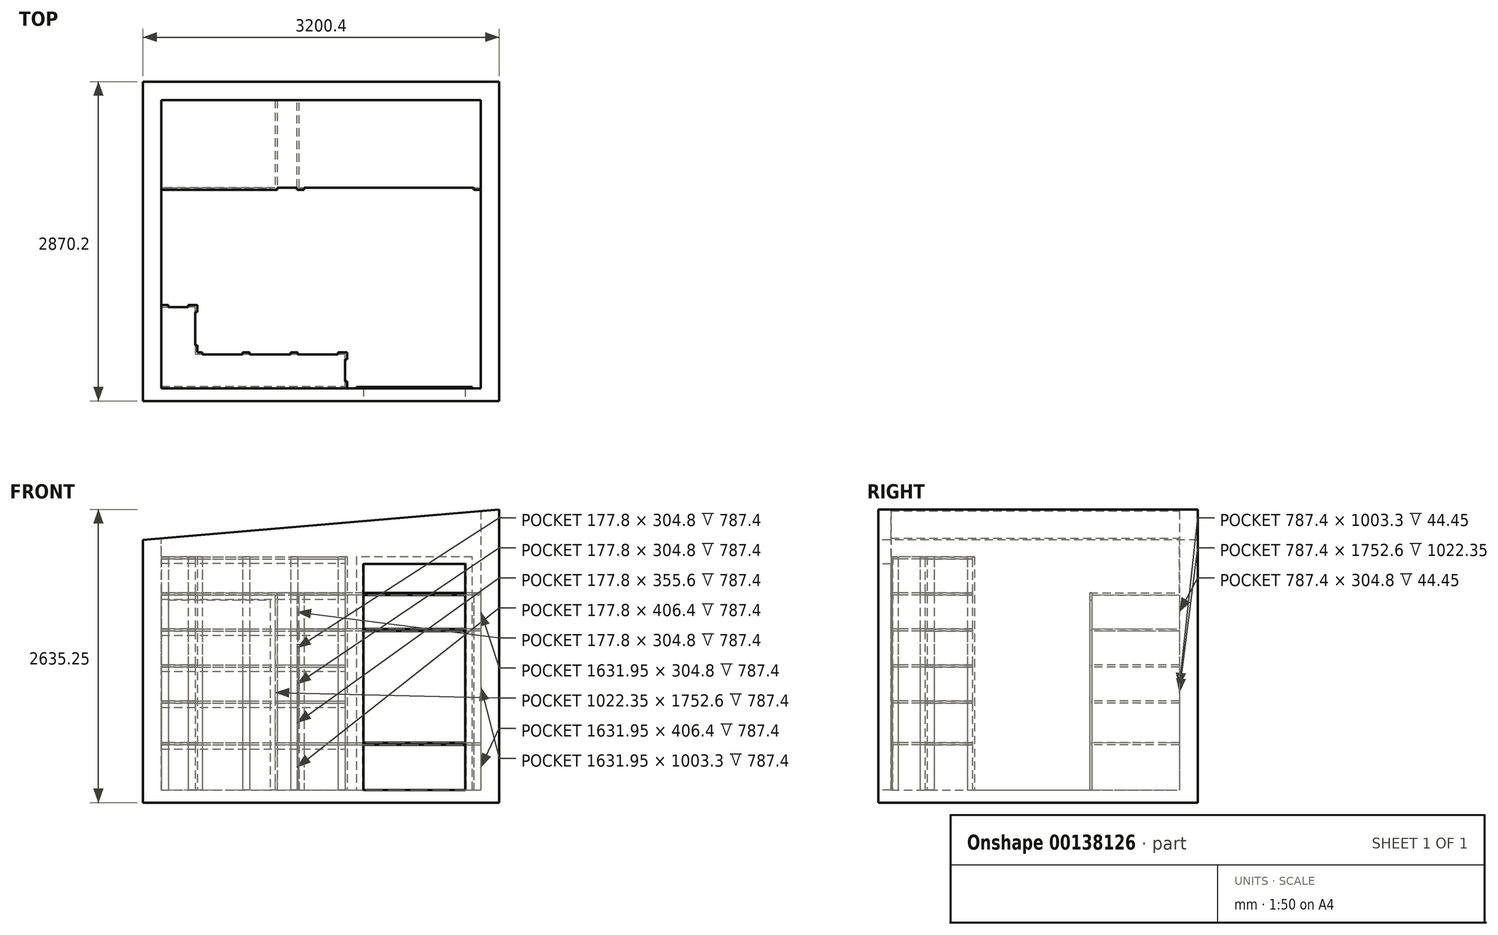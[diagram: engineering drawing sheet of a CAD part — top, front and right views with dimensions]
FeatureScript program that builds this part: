
annotation { "Feature Type Name" : "Feature", "Feature Type Description" : "" }
export const myFeature = defineFeature(function(context is Context, id is Id, definition is map)
    precondition{}
    {
        {
            var Q0;
            Q0=qCreatedBy(makeId("Right.planeOp"),FACE);
            var sketch = newSketch(context, id + "F0", { "sketchPlane" : qUnion([Q0])});
            skLineSegment(sketch, "E0.bottom", {"start": v(0, 0) * mm, "end": v(2590.8, 0) * mm});
            skLineSegment(sketch, "E0.top", {"start": v(0, 2520.95) * mm, "end": v(2590.8, 2520.95) * mm});
            skLineSegment(sketch, "E0.left", {"start": v(0, 0) * mm, "end": v(0, 2520.95) * mm});
            skLineSegment(sketch, "E0.right", {"start": v(2590.8, 0) * mm, "end": v(2590.8, 2520.95) * mm});
            skSolve(sketch);
        }
        {
            var Q0;
            Q0=qSketchRegion(id+"F0",true);
            extrude(context, id + "F1", {"entities" : qUnion([Q0]), "depth" : 165.1 * mm});
        }
        {
            var Q0;
            Q0=makeQuery(id+"F1.opExtrude","SWEPT_FACE",FACE,{"disambiguationData":[OSD([sQuery(id+"F0.wireOp",EDGE,"E0.left")])]});
            var sketch = newSketch(context, id + "F2", { "sketchPlane" : qUnion([Q0])});
            skLineSegment(sketch, "E1.bottom", {"start": v(0, 2520.95) * mm, "end": v(3035.3, 2520.95) * mm});
            skLineSegment(sketch, "E1.top", {"start": v(0, 0) * mm, "end": v(3035.3, 0) * mm});
            skLineSegment(sketch, "E1.left", {"start": v(0, 2520.95) * mm, "end": v(0, 0) * mm});
            skLineSegment(sketch, "E1.right", {"start": v(3035.3, 2520.95) * mm, "end": v(3035.3, 0) * mm});
            skSolve(sketch);
        }
        {
            var Q0;
            Q0=qSketchRegion(id+"F2",true);
            extrude(context, id + "F3", {"entities" : qUnion([Q0]), "operationType" : NewBodyOperationType.ADD, "depth" : 114.3 * mm});
        }
        {
            var Q0;
            Q0=makeQuery(id+"F1.opExtrude","SWEPT_FACE",FACE,{"disambiguationData":[OSD([sQuery(id+"F0.wireOp",EDGE,"E0.right")])]});
            var sketch = newSketch(context, id + "F4", { "sketchPlane" : qUnion([Q0])});
            skLineSegment(sketch, "E2.bottom", {"start": v(0, 2520.95) * mm, "end": v(-3035.3, 2520.95) * mm});
            skLineSegment(sketch, "E2.top", {"start": v(0, 0) * mm, "end": v(-3035.3, 0) * mm});
            skLineSegment(sketch, "E2.left", {"start": v(0, 2520.95) * mm, "end": v(0, 0) * mm});
            skLineSegment(sketch, "E2.right", {"start": v(-3035.3, 2520.95) * mm, "end": v(-3035.3, 0) * mm});
            skSolve(sketch);
        }
        {
            var Q0;
            Q0=qSketchRegion(id+"F4",true);
            extrude(context, id + "F5", {"entities" : qUnion([Q0]), "operationType" : NewBodyOperationType.ADD, "depth" : 165.1 * mm});
        }
        {
            var Q0;
            Q0=makeQuery(id+"F3.opExtrude","SWEPT_FACE",FACE,{"disambiguationData":[OSD([sQuery(id+"F2.wireOp",EDGE,"E1.right")])]});
            var sketch = newSketch(context, id + "F6", { "sketchPlane" : qUnion([Q0])});
            skLineSegment(sketch, "E3.bottom", {"start": v(-114.3, 2520.95) * mm, "end": v(2755.9, 2520.95) * mm});
            skLineSegment(sketch, "E3.top", {"start": v(-114.3, 0) * mm, "end": v(2755.9, 0) * mm});
            skLineSegment(sketch, "E3.left", {"start": v(-114.3, 2520.95) * mm, "end": v(-114.3, 0) * mm});
            skLineSegment(sketch, "E3.right", {"start": v(2755.9, 2520.95) * mm, "end": v(2755.9, 0) * mm});
            skSolve(sketch);
        }
        {
            var Q0;
            Q0=qSketchRegion(id+"F6",true);
            extrude(context, id + "F7", {"entities" : qUnion([Q0]), "operationType" : NewBodyOperationType.ADD, "depth" : 165.1 * mm});
        }
        {
            var Q0;
            Q0=makeQuery(id+"F7.boolean.opBoolean","MERGE",FACE,{"derivedFrom":[makeQuery(id+"F3.opExtrude","CAP_FACE",FACE,{"disambiguationData":[OSD([sQuery(id+"F2.wireOp",EDGE,"E1.bottom"),sQuery(id+"F2.wireOp",EDGE,"E1.top"),sQuery(id+"F2.wireOp",EDGE,"E1.left"),sQuery(id+"F2.wireOp",EDGE,"E1.right")])],"isStart":false}),makeQuery(id+"F7.opExtrude","SWEPT_FACE",FACE,{"disambiguationData":[OSD([sQuery(id+"F6.wireOp",EDGE,"E3.left")])]})]});
            var sketch = newSketch(context, id + "F8", { "sketchPlane" : qUnion([Q0])});
            skLineSegment(sketch, "E4.bottom", {"start": v(2895.6, 0) * mm, "end": v(1981.2, 0) * mm});
            skLineSegment(sketch, "E4.top", {"start": v(2895.6, 2032) * mm, "end": v(1981.2, 2032) * mm});
            skLineSegment(sketch, "E4.left", {"start": v(2895.6, 0) * mm, "end": v(2895.6, 2032) * mm});
            skLineSegment(sketch, "E4.right", {"start": v(1981.2, 0) * mm, "end": v(1981.2, 2032) * mm});
            skSolve(sketch);
        }
        {
            var Q0;
            Q0=makeQuery(id+"F8.imprint","IMPRINT",FACE,{"disambiguationData":[TD([[makeQuery(id+"F8.imprint","IMPRINT",EDGE,{"derivedFrom":sQuery(id+"F8.wireOp",EDGE,"E4.top")}),-1.0]])]});
            var sketch = newSketch(context, id + "F9", { "sketchPlane" : qUnion([Q0])});
            skLineSegment(sketch, "E5", {"start": v(0, 2247.9) * mm, "end": v(3200.4, 2520.95) * mm});
            skLineSegment(sketch, "E6", {"start": v(3200.4, 2520.95) * mm, "end": v(0, 2520.95) * mm});
            skLineSegment(sketch, "E7", {"start": v(0, 2520.95) * mm, "end": v(0, 2247.9) * mm});
            skSolve(sketch);
        }
        {
            var Q0;
            Q0=qSketchRegion(id+"F9",true);
            extrude(context, id + "F10", {"entities" : qUnion([Q0]), "operationType" : NewBodyOperationType.REMOVE, "endBound" : BoundingType.THROUGH_ALL, "oppositeDirection" : true, "depth" : 25.4 * mm});
        }
        {
            var Q0;
            Q0=qSketchRegion(id+"F8",true);
            extrude(context, id + "F11", {"entities" : qUnion([Q0]), "operationType" : NewBodyOperationType.REMOVE, "oppositeDirection" : true, "depth" : 114.3 * mm});
        }
        {
            var Q0;
            Q0=makeQuery(id+"F7.boolean.opBoolean","MERGE",FACE,{"derivedFrom":[makeQuery(id+"F5.boolean.opBoolean","MERGE",FACE,{"derivedFrom":[makeQuery(id+"F3.boolean.opBoolean","MERGE",FACE,{"derivedFrom":[makeQuery(id+"F1.opExtrude","SWEPT_FACE",FACE,{"disambiguationData":[OSD([sQuery(id+"F0.wireOp",EDGE,"E0.bottom")])]}),makeQuery(id+"F3.opExtrude","SWEPT_FACE",FACE,{"disambiguationData":[OSD([sQuery(id+"F2.wireOp",EDGE,"E1.top")])]})]}),makeQuery(id+"F5.opExtrude","SWEPT_FACE",FACE,{"disambiguationData":[OSD([sQuery(id+"F4.wireOp",EDGE,"E2.top")])]})]}),makeQuery(id+"F7.opExtrude","SWEPT_FACE",FACE,{"disambiguationData":[OSD([sQuery(id+"F6.wireOp",EDGE,"E3.top")])]})]});
            var sketch = newSketch(context, id + "F12", { "sketchPlane" : qUnion([Q0])});
            skLineSegment(sketch, "E8.bottom", {"start": v(0, 114.3) * mm, "end": v(3200.4, 114.3) * mm});
            skLineSegment(sketch, "E8.top", {"start": v(0, -2755.9) * mm, "end": v(3200.4, -2755.9) * mm});
            skLineSegment(sketch, "E8.left", {"start": v(0, 114.3) * mm, "end": v(0, -2755.9) * mm});
            skLineSegment(sketch, "E8.right", {"start": v(3200.4, 114.3) * mm, "end": v(3200.4, -2755.9) * mm});
            skSolve(sketch);
        }
        {
            var Q0;
            Q0=qSketchRegion(id+"F12",true);
            extrude(context, id + "F13", {"entities" : qUnion([Q0]), "operationType" : NewBodyOperationType.ADD, "depth" : 114.3 * mm});
        }
        {
            var Q0;
            Q0=makeQuery(id+"F3.opExtrude","CAP_FACE",FACE,{"disambiguationData":[OSD([sQuery(id+"F2.wireOp",EDGE,"E1.bottom"),sQuery(id+"F2.wireOp",EDGE,"E1.top"),sQuery(id+"F2.wireOp",EDGE,"E1.left"),sQuery(id+"F2.wireOp",EDGE,"E1.right")])],"isStart":true});
            var sketch = newSketch(context, id + "F14", { "sketchPlane" : qUnion([Q0])});
            skLineSegment(sketch, "E9", {"start": v(-1974.85, 0) * mm, "end": v(-1974.85, 2038.35) * mm});
            skLineSegment(sketch, "E10", {"start": v(-1974.85, 2038.35) * mm, "end": v(-2901.95, 2038.35) * mm});
            skLineSegment(sketch, "E11", {"start": v(-2901.95, 2038.35) * mm, "end": v(-2901.95, 0) * mm});
            skPoint(sketch, "E11.endSnap0", {"position": v(-2965.45, 0) * mm});
            skLineSegment(sketch, "E12", {"start": v(-2901.95, 0) * mm, "end": v(-2959.1, 0) * mm});
            skLineSegment(sketch, "E13", {"start": v(-2959.1, 0) * mm, "end": v(-2959.1, 2095.5) * mm});
            skLineSegment(sketch, "E14", {"start": v(-2959.1, 2095.5) * mm, "end": v(-1917.7, 2095.5) * mm});
            skLineSegment(sketch, "E15", {"start": v(-1917.7, 2095.5) * mm, "end": v(-1917.7, 0) * mm});
            skLineSegment(sketch, "E16", {"start": v(-1917.7, 0) * mm, "end": v(-1974.85, 0) * mm});
            skSolve(sketch);
        }
        {
            var Q0;
            Q0=qSketchRegion(id+"F14",true);
            extrude(context, id + "F15", {"entities" : qUnion([Q0]), "operationType" : NewBodyOperationType.ADD, "depth" : 12.7 * mm});
        }
        {
            var Q0;
            Q0=makeQuery(id+"F15.boolean.opBoolean","SPLIT",FACE,{"disambiguationData":[TD([makeQuery(id+"F10.boolean.opBoolean","COPY",FACE,{"derivedFrom":makeQuery(id+"F10.opExtrude","SWEPT_FACE",FACE,{"disambiguationData":[OSD([sQuery(id+"F9.wireOp",EDGE,"E5")])]})})])],"derivedFrom":makeQuery(id+"F3.opExtrude","CAP_FACE",FACE,{"disambiguationData":[OSD([sQuery(id+"F2.wireOp",EDGE,"E1.bottom"),sQuery(id+"F2.wireOp",EDGE,"E1.top"),sQuery(id+"F2.wireOp",EDGE,"E1.left"),sQuery(id+"F2.wireOp",EDGE,"E1.right")])],"isStart":true})});
            var Q1;
            Q1=makeQuery(id+"F13.boolean.opBoolean","MERGE",FACE,{"derivedFrom":[makeQuery(id+"F7.boolean.opBoolean","MERGE",FACE,{"derivedFrom":[makeQuery(id+"F3.opExtrude","CAP_FACE",FACE,{"disambiguationData":[OSD([sQuery(id+"F2.wireOp",EDGE,"E1.bottom"),sQuery(id+"F2.wireOp",EDGE,"E1.top"),sQuery(id+"F2.wireOp",EDGE,"E1.left"),sQuery(id+"F2.wireOp",EDGE,"E1.right")])],"isStart":false}),makeQuery(id+"F7.opExtrude","SWEPT_FACE",FACE,{"disambiguationData":[OSD([sQuery(id+"F6.wireOp",EDGE,"E3.left")])]})]}),makeQuery(id+"F13.opExtrude","SWEPT_FACE",FACE,{"disambiguationData":[OSD([sQuery(id+"F12.wireOp",EDGE,"E8.bottom")])]})]});
            cPlane(context, id + "F16", {"entities" : qUnion([Q0, Q1]), "cplaneType" : CPlaneType.MID_PLANE, "offset" : 25.4 * mm, "width" : 152.4 * mm, "height" : 152.4 * mm});
        }
        {
            var Q0;
            Q0=makeQuery(id+"F13.opExtrude","CAP_FACE",FACE,{"disambiguationData":[OSD([sQuery(id+"F12.wireOp",EDGE,"E8.bottom"),sQuery(id+"F12.wireOp",EDGE,"E8.top"),sQuery(id+"F12.wireOp",EDGE,"E8.left"),sQuery(id+"F12.wireOp",EDGE,"E8.right")])],"isStart":true});
            var sketch = newSketch(context, id + "F17", { "sketchPlane" : qUnion([Q0])});
            skLineSegment(sketch, "E17.bottom", {"start": v(3200.4, 304.8) * mm, "end": v(469.9, 304.8) * mm});
            skLineSegment(sketch, "E17.top", {"start": v(3200.4, 2755.9) * mm, "end": v(469.9, 2755.9) * mm});
            skLineSegment(sketch, "E17.left", {"start": v(3200.4, 304.8) * mm, "end": v(3200.4, 2755.9) * mm});
            skLineSegment(sketch, "E17.right", {"start": v(469.9, 304.8) * mm, "end": v(469.9, 2755.9) * mm});
            skSolve(sketch);
        }
        {
            var Q0;
            Q0=makeQuery(id+"F15.boolean.opBoolean","SPLIT",FACE,{"disambiguationData":[TD([makeQuery(id+"F10.boolean.opBoolean","COPY",FACE,{"derivedFrom":makeQuery(id+"F10.opExtrude","SWEPT_FACE",FACE,{"disambiguationData":[OSD([sQuery(id+"F9.wireOp",EDGE,"E5")])]})})])],"derivedFrom":makeQuery(id+"F3.opExtrude","CAP_FACE",FACE,{"disambiguationData":[OSD([sQuery(id+"F2.wireOp",EDGE,"E1.bottom"),sQuery(id+"F2.wireOp",EDGE,"E1.top"),sQuery(id+"F2.wireOp",EDGE,"E1.left"),sQuery(id+"F2.wireOp",EDGE,"E1.right")])],"isStart":true})});
            var sketch = newSketch(context, id + "F18", { "sketchPlane" : qUnion([Q0])});
            skLineSegment(sketch, "E18.bottom", {"start": v(-165.1, 406.4) * mm, "end": v(-1816.1, 406.4) * mm});
            skLineSegment(sketch, "E18.top", {"start": v(-165.1, 425.45) * mm, "end": v(-1816.1, 425.45) * mm});
            skLineSegment(sketch, "E18.left", {"start": v(-165.1, 406.4) * mm, "end": v(-165.1, 425.45) * mm});
            skLineSegment(sketch, "E18.right", {"start": v(-1816.1, 406.4) * mm, "end": v(-1816.1, 425.45) * mm});
            skLineSegment(sketch, "E19.bottom", {"start": v(-165.1, 781.05) * mm, "end": v(-1816.1, 781.05) * mm});
            skLineSegment(sketch, "E19.top", {"start": v(-165.1, 800.1) * mm, "end": v(-1816.1, 800.1) * mm});
            skLineSegment(sketch, "E19.left", {"start": v(-165.1, 781.05) * mm, "end": v(-165.1, 800.1) * mm});
            skLineSegment(sketch, "E19.right", {"start": v(-1816.1, 781.05) * mm, "end": v(-1816.1, 800.1) * mm});
            skLineSegment(sketch, "E20.bottom", {"start": v(-165.1, 1104.9) * mm, "end": v(-1816.1, 1104.9) * mm});
            skLineSegment(sketch, "E20.top", {"start": v(-165.1, 1123.95) * mm, "end": v(-1816.1, 1123.95) * mm});
            skLineSegment(sketch, "E20.left", {"start": v(-165.1, 1104.9) * mm, "end": v(-165.1, 1123.95) * mm});
            skLineSegment(sketch, "E20.right", {"start": v(-1816.1, 1104.9) * mm, "end": v(-1816.1, 1123.95) * mm});
            skLineSegment(sketch, "E21.bottom", {"start": v(-165.1, 1428.75) * mm, "end": v(-1816.1, 1428.75) * mm});
            skLineSegment(sketch, "E21.top", {"start": v(-165.1, 1447.8) * mm, "end": v(-1816.1, 1447.8) * mm});
            skLineSegment(sketch, "E21.left", {"start": v(-165.1, 1428.75) * mm, "end": v(-165.1, 1447.8) * mm});
            skLineSegment(sketch, "E21.right", {"start": v(-1816.1, 1428.75) * mm, "end": v(-1816.1, 1447.8) * mm});
            skLineSegment(sketch, "E22.bottom", {"start": v(-165.1, 1752.6) * mm, "end": v(-1816.1, 1752.6) * mm});
            skLineSegment(sketch, "E22.top", {"start": v(-165.1, 1771.65) * mm, "end": v(-1816.1, 1771.65) * mm});
            skLineSegment(sketch, "E22.left", {"start": v(-165.1, 1752.6) * mm, "end": v(-165.1, 1771.65) * mm});
            skLineSegment(sketch, "E22.right", {"start": v(-1816.1, 1752.6) * mm, "end": v(-1816.1, 1771.65) * mm});
            skLineSegment(sketch, "E23.bottom", {"start": v(-165.1, 2076.45) * mm, "end": v(-1816.1, 2076.45) * mm});
            skLineSegment(sketch, "E23.top", {"start": v(-165.1, 2095.5) * mm, "end": v(-1816.1, 2095.5) * mm});
            skLineSegment(sketch, "E23.left", {"start": v(-165.1, 2076.45) * mm, "end": v(-165.1, 2095.5) * mm});
            skLineSegment(sketch, "E23.right", {"start": v(-1816.1, 2076.45) * mm, "end": v(-1816.1, 2095.5) * mm});
            skSolve(sketch);
        }
        {
            var Q0;
            Q0=qSketchRegion(id+"F18",true);
            extrude(context, id + "F19", {"entities" : qUnion([Q0]), "operationType" : NewBodyOperationType.ADD, "depth" : 304.8 * mm});
        }
        {
            var Q0;
            Q0=makeQuery(id+"F15.boolean.opBoolean","SPLIT",FACE,{"disambiguationData":[TD([makeQuery(id+"F10.boolean.opBoolean","COPY",FACE,{"derivedFrom":makeQuery(id+"F10.opExtrude","SWEPT_FACE",FACE,{"disambiguationData":[OSD([sQuery(id+"F9.wireOp",EDGE,"E5")])]})})])],"derivedFrom":makeQuery(id+"F3.opExtrude","CAP_FACE",FACE,{"disambiguationData":[OSD([sQuery(id+"F2.wireOp",EDGE,"E1.bottom"),sQuery(id+"F2.wireOp",EDGE,"E1.top"),sQuery(id+"F2.wireOp",EDGE,"E1.left"),sQuery(id+"F2.wireOp",EDGE,"E1.right")])],"isStart":true})});
            var sketch = newSketch(context, id + "F20", { "sketchPlane" : qUnion([Q0])});
            skLineSegment(sketch, "E24.bottom", {"start": v(-165.1, 2076.45) * mm, "end": v(-1816.1, 2076.45) * mm});
            skLineSegment(sketch, "E24.top", {"start": v(-165.1, 2038.35) * mm, "end": v(-1816.1, 2038.35) * mm});
            skLineSegment(sketch, "E24.left", {"start": v(-165.1, 2076.45) * mm, "end": v(-165.1, 2038.35) * mm});
            skLineSegment(sketch, "E24.right", {"start": v(-1816.1, 2076.45) * mm, "end": v(-1816.1, 2038.35) * mm});
            skLineSegment(sketch, "E25.bottom", {"start": v(-165.1, 1752.6) * mm, "end": v(-1816.1, 1752.6) * mm});
            skLineSegment(sketch, "E25.top", {"start": v(-165.1, 1714.5) * mm, "end": v(-1816.1, 1714.5) * mm});
            skLineSegment(sketch, "E25.left", {"start": v(-165.1, 1752.6) * mm, "end": v(-165.1, 1714.5) * mm});
            skLineSegment(sketch, "E25.right", {"start": v(-1816.1, 1752.6) * mm, "end": v(-1816.1, 1714.5) * mm});
            skLineSegment(sketch, "E26.bottom", {"start": v(-165.1, 1428.75) * mm, "end": v(-1816.1, 1428.75) * mm});
            skLineSegment(sketch, "E26.top", {"start": v(-165.1, 1390.65) * mm, "end": v(-1816.1, 1390.65) * mm});
            skLineSegment(sketch, "E26.left", {"start": v(-165.1, 1428.75) * mm, "end": v(-165.1, 1390.65) * mm});
            skLineSegment(sketch, "E26.right", {"start": v(-1816.1, 1428.75) * mm, "end": v(-1816.1, 1390.65) * mm});
            skLineSegment(sketch, "E27.bottom", {"start": v(-165.1, 1104.9) * mm, "end": v(-1816.1, 1104.9) * mm});
            skLineSegment(sketch, "E27.top", {"start": v(-165.1, 1066.8) * mm, "end": v(-1816.1, 1066.8) * mm});
            skLineSegment(sketch, "E27.left", {"start": v(-165.1, 1104.9) * mm, "end": v(-165.1, 1066.8) * mm});
            skLineSegment(sketch, "E27.right", {"start": v(-1816.1, 1104.9) * mm, "end": v(-1816.1, 1066.8) * mm});
            skLineSegment(sketch, "E28.bottom", {"start": v(-165.1, 406.4) * mm, "end": v(-1816.1, 406.4) * mm});
            skLineSegment(sketch, "E28.top", {"start": v(-165.1, 368.3) * mm, "end": v(-1816.1, 368.3) * mm});
            skLineSegment(sketch, "E28.left", {"start": v(-165.1, 406.4) * mm, "end": v(-165.1, 368.3) * mm});
            skLineSegment(sketch, "E28.right", {"start": v(-1816.1, 406.4) * mm, "end": v(-1816.1, 368.3) * mm});
            skLineSegment(sketch, "E29.bottom", {"start": v(-165.1, 781.05) * mm, "end": v(-1816.1, 781.05) * mm});
            skLineSegment(sketch, "E29.top", {"start": v(-165.1, 742.95) * mm, "end": v(-1816.1, 742.95) * mm});
            skLineSegment(sketch, "E29.left", {"start": v(-165.1, 781.05) * mm, "end": v(-165.1, 742.95) * mm});
            skLineSegment(sketch, "E29.right", {"start": v(-1816.1, 781.05) * mm, "end": v(-1816.1, 742.95) * mm});
            skSolve(sketch);
        }
        {
            var Q0;
            Q0=qSketchRegion(id+"F20",true);
            extrude(context, id + "F21", {"entities" : qUnion([Q0]), "operationType" : NewBodyOperationType.ADD, "depth" : 19.05 * mm});
        }
        {
            var Q0;
            Q0=makeQuery(id+"Fllte4z2JdaSj08_1.boolean.opBoolean","MERGE",FACE,{"derivedFrom":[makeQuery(id+"F13.opExtrude","CAP_FACE",FACE,{"disambiguationData":[OSD([sQuery(id+"F12.wireOp",EDGE,"E8.bottom"),sQuery(id+"F12.wireOp",EDGE,"E8.top"),sQuery(id+"F12.wireOp",EDGE,"E8.left"),sQuery(id+"F12.wireOp",EDGE,"E8.right")])],"isStart":true}),makeQuery(id+"Fllte4z2JdaSj08_1.opExtrude","CAP_FACE",FACE,{"disambiguationData":[OSD([sQuery(id+"F17.wireOp",EDGE,"E17.bottom"),sQuery(id+"F17.wireOp",EDGE,"E17.top"),sQuery(id+"F17.wireOp",EDGE,"E17.left"),sQuery(id+"F17.wireOp",EDGE,"E17.right")])],"isStart":true})]});
            var sketch = newSketch(context, id + "F22", { "sketchPlane" : qUnion([Q0])});
            skLineSegment(sketch, "E30.bottom", {"start": v(1835.15, 0) * mm, "end": v(1816.1, 0) * mm});
            skLineSegment(sketch, "E30.top", {"start": v(1835.15, 63.5) * mm, "end": v(1816.1, 63.5) * mm});
            skLineSegment(sketch, "E30.left", {"start": v(1835.15, 0) * mm, "end": v(1835.15, 63.5) * mm});
            skLineSegment(sketch, "E30.right", {"start": v(1816.1, 0) * mm, "end": v(1816.1, 63.5) * mm});
            skLineSegment(sketch, "E31.bottom", {"start": v(1835.15, 260.35) * mm, "end": v(1816.1, 260.35) * mm});
            skLineSegment(sketch, "E31.top", {"start": v(1835.15, 323.85) * mm, "end": v(1816.1, 323.85) * mm});
            skLineSegment(sketch, "E31.left", {"start": v(1835.15, 260.35) * mm, "end": v(1835.15, 323.85) * mm});
            skLineSegment(sketch, "E31.right", {"start": v(1816.1, 260.35) * mm, "end": v(1816.1, 323.85) * mm});
            skLineSegment(sketch, "E32.bottom", {"start": v(1816.1, 323.85) * mm, "end": v(1752.6, 323.85) * mm});
            skLineSegment(sketch, "E32.top", {"start": v(1816.1, 304.8) * mm, "end": v(1752.6, 304.8) * mm});
            skLineSegment(sketch, "E32.left", {"start": v(1816.1, 323.85) * mm, "end": v(1816.1, 304.8) * mm});
            skLineSegment(sketch, "E32.right", {"start": v(1752.6, 323.85) * mm, "end": v(1752.6, 304.8) * mm});
            skLineSegment(sketch, "E33.bottom", {"start": v(1390.65, 323.85) * mm, "end": v(1327.15, 323.85) * mm});
            skLineSegment(sketch, "E33.top", {"start": v(1390.65, 304.8) * mm, "end": v(1327.15, 304.8) * mm});
            skLineSegment(sketch, "E33.left", {"start": v(1390.65, 323.85) * mm, "end": v(1390.65, 304.8) * mm});
            skLineSegment(sketch, "E33.right", {"start": v(1327.15, 323.85) * mm, "end": v(1327.15, 304.8) * mm});
            skLineSegment(sketch, "E34.bottom", {"start": v(533.4, 323.85) * mm, "end": v(469.9, 323.85) * mm});
            skLineSegment(sketch, "E34.top", {"start": v(533.4, 304.8) * mm, "end": v(469.9, 304.8) * mm});
            skLineSegment(sketch, "E34.left", {"start": v(533.4, 323.85) * mm, "end": v(533.4, 304.8) * mm});
            skLineSegment(sketch, "E34.right", {"start": v(469.9, 323.85) * mm, "end": v(469.9, 304.8) * mm});
            skLineSegment(sketch, "E35.bottom", {"start": v(469.9, 323.85) * mm, "end": v(488.95, 323.85) * mm});
            skLineSegment(sketch, "E35.top", {"start": v(469.9, 387.35) * mm, "end": v(488.95, 387.35) * mm});
            skLineSegment(sketch, "E35.left", {"start": v(469.9, 323.85) * mm, "end": v(469.9, 387.35) * mm});
            skLineSegment(sketch, "E35.right", {"start": v(488.95, 323.85) * mm, "end": v(488.95, 387.35) * mm});
            skLineSegment(sketch, "E36.bottom", {"start": v(958.85, 304.8) * mm, "end": v(895.35, 304.8) * mm});
            skLineSegment(sketch, "E36.top", {"start": v(958.85, 323.85) * mm, "end": v(895.35, 323.85) * mm});
            skLineSegment(sketch, "E36.left", {"start": v(958.85, 304.8) * mm, "end": v(958.85, 323.85) * mm});
            skLineSegment(sketch, "E36.right", {"start": v(895.35, 304.8) * mm, "end": v(895.35, 323.85) * mm});
            skSolve(sketch);
        }
        {
            var Q0;
            Q0=qSketchRegion(id+"F22",true);
            extrude(context, id + "F23", {"entities" : qUnion([Q0]), "operationType" : NewBodyOperationType.ADD, "depth" : 2095.5 * mm});
        }
        {
            var Q0;
            Q0=makeQuery(id+"F1.opExtrude","CAP_FACE",FACE,{"disambiguationData":[OSD([sQuery(id+"F0.wireOp",EDGE,"E0.bottom"),sQuery(id+"F0.wireOp",EDGE,"E0.top"),sQuery(id+"F0.wireOp",EDGE,"E0.left"),sQuery(id+"F0.wireOp",EDGE,"E0.right")])],"isStart":false});
            var sketch = newSketch(context, id + "F24", { "sketchPlane" : qUnion([Q0])});
            skPoint(sketch, "E37.oppositeSnap0", {"position": v(161.93, 2076.45) * mm});
            skLineSegment(sketch, "E37.bottom", {"start": v(304.8, 2095.5) * mm, "end": v(2590.8, 2095.5) * mm});
            skLineSegment(sketch, "E37.top", {"start": v(304.8, 2076.45) * mm, "end": v(2590.8, 2076.45) * mm});
            skLineSegment(sketch, "E37.left", {"start": v(304.8, 2095.5) * mm, "end": v(304.8, 2076.45) * mm});
            skLineSegment(sketch, "E37.right", {"start": v(2590.8, 2095.5) * mm, "end": v(2590.8, 2076.45) * mm});
            skLineSegment(sketch, "E38.bottom", {"start": v(304.8, 1771.65) * mm, "end": v(2590.8, 1771.65) * mm});
            skLineSegment(sketch, "E38.top", {"start": v(304.8, 1752.6) * mm, "end": v(2590.8, 1752.6) * mm});
            skLineSegment(sketch, "E38.left", {"start": v(304.8, 1771.65) * mm, "end": v(304.8, 1752.6) * mm});
            skLineSegment(sketch, "E38.right", {"start": v(2590.8, 1771.65) * mm, "end": v(2590.8, 1752.6) * mm});
            skLineSegment(sketch, "E39.bottom", {"start": v(304.8, 1447.8) * mm, "end": v(2590.8, 1447.8) * mm});
            skLineSegment(sketch, "E39.top", {"start": v(304.8, 1428.75) * mm, "end": v(2590.8, 1428.75) * mm});
            skLineSegment(sketch, "E39.left", {"start": v(304.8, 1447.8) * mm, "end": v(304.8, 1428.75) * mm});
            skLineSegment(sketch, "E39.right", {"start": v(2590.8, 1447.8) * mm, "end": v(2590.8, 1428.75) * mm});
            skLineSegment(sketch, "E40.bottom", {"start": v(304.8, 425.45) * mm, "end": v(2590.8, 425.45) * mm});
            skLineSegment(sketch, "E40.top", {"start": v(304.8, 406.4) * mm, "end": v(2590.8, 406.4) * mm});
            skLineSegment(sketch, "E40.left", {"start": v(304.8, 425.45) * mm, "end": v(304.8, 406.4) * mm});
            skLineSegment(sketch, "E40.right", {"start": v(2590.8, 425.45) * mm, "end": v(2590.8, 406.4) * mm});
            skLineSegment(sketch, "E41.bottom", {"start": v(304.8, 800.1) * mm, "end": v(2590.8, 800.1) * mm});
            skLineSegment(sketch, "E41.top", {"start": v(304.8, 781.05) * mm, "end": v(2590.8, 781.05) * mm});
            skLineSegment(sketch, "E41.left", {"start": v(304.8, 800.1) * mm, "end": v(304.8, 781.05) * mm});
            skLineSegment(sketch, "E41.right", {"start": v(2590.8, 800.1) * mm, "end": v(2590.8, 781.05) * mm});
            skLineSegment(sketch, "E42.bottom", {"start": v(304.8, 1123.95) * mm, "end": v(2590.8, 1123.95) * mm});
            skLineSegment(sketch, "E42.top", {"start": v(304.8, 1104.9) * mm, "end": v(2590.8, 1104.9) * mm});
            skLineSegment(sketch, "E42.left", {"start": v(304.8, 1123.95) * mm, "end": v(304.8, 1104.9) * mm});
            skLineSegment(sketch, "E42.right", {"start": v(2590.8, 1123.95) * mm, "end": v(2590.8, 1104.9) * mm});
            skSolve(sketch);
        }
        {
            var Q0;
            Q0=qSketchRegion(id+"F24",true);
            extrude(context, id + "F25", {"entities" : qUnion([Q0]), "operationType" : NewBodyOperationType.ADD, "depth" : 304.8 * mm});
        }
        {
            var Q0;
            Q0=makeQuery(id+"FbiakTUjsby0JHI_1.boolean.opBoolean","MERGE",FACE,{"derivedFrom":[makeQuery(id+"F25.boolean.opBoolean","MERGE",FACE,{"derivedFrom":[makeQuery(id+"F19.opExtrude","SWEPT_FACE",FACE,{"disambiguationData":[OSD([sQuery(id+"F18.wireOp",EDGE,"E18.top")])]}),makeQuery(id+"F25.opExtrude","SWEPT_FACE",FACE,{"disambiguationData":[OSD([sQuery(id+"F24.wireOp",EDGE,"E40.bottom")])]})]}),makeQuery(id+"FbiakTUjsby0JHI_1.opExtrude","SWEPT_FACE",FACE,{"disambiguationData":[OSD([sQuery(id+"FjrpZ5JBxR4FeDl_1.wireOp",EDGE,"Qz6daa4T-fzVh-TU3N-sVul-O9IAGAUrbKFN.bottom")])]})]});
            var sketch = newSketch(context, id + "F26", { "sketchPlane" : qUnion([Q0])});
            skLineSegment(sketch, "E43.bottom", {"start": v(622.3, 2590.8) * mm, "end": v(2044.7, 2590.8) * mm});
            skLineSegment(sketch, "E43.top", {"start": v(622.3, 1803.4) * mm, "end": v(2044.7, 1803.4) * mm});
            skLineSegment(sketch, "E43.left", {"start": v(622.3, 2590.8) * mm, "end": v(622.3, 1803.4) * mm});
            skLineSegment(sketch, "E43.right", {"start": v(2044.7, 2590.8) * mm, "end": v(2044.7, 1803.4) * mm});
            skLineSegment(sketch, "E44.bottom", {"start": v(2044.7, 2590.8) * mm, "end": v(3035.3, 2590.8) * mm});
            skLineSegment(sketch, "E44.top", {"start": v(2044.7, 1803.4) * mm, "end": v(3035.3, 1803.4) * mm});
            skLineSegment(sketch, "E44.right", {"start": v(3035.3, 2590.8) * mm, "end": v(3035.3, 1803.4) * mm});
            skSolve(sketch);
        }
        {
            var Q0;
            Q0=qSketchRegion(id+"F26",true);
            extrude(context, id + "F27", {"entities" : qUnion([Q0]), "operationType" : NewBodyOperationType.REMOVE, "depth" : 990.6 * mm});
        }
        {
            var Q0;
            {var subQ0=sQuery(id+"F17.wireOp",EDGE,"E17.right");var subQ1=sQuery(id+"F17.wireOp",EDGE,"E17.bottom");var subQ2=makeQuery(id+"F17.imprint","INTERSECT",VERTEX,{"derivedFrom":[subQ1,subQ0]});Q0=makeQuery(id+"F17.imprint","IMPRINT",FACE,{"disambiguationData":[TD([[makeQuery(id+"F17.imprint","IMPRINT",EDGE,{"disambiguationData":[TD([[subQ2,1.0]])],"derivedFrom":subQ1}),-1.0]])]});}
            var sketch = newSketch(context, id + "F28", { "sketchPlane" : qUnion([Q0])});
            skLineSegment(sketch, "E45.bottom", {"start": v(1403.35, 1803.4) * mm, "end": v(1384.3, 1803.4) * mm});
            skLineSegment(sketch, "E45.top", {"start": v(1403.35, 2590.8) * mm, "end": v(1384.3, 2590.8) * mm});
            skLineSegment(sketch, "E45.left", {"start": v(1403.35, 1803.4) * mm, "end": v(1403.35, 2590.8) * mm});
            skLineSegment(sketch, "E45.right", {"start": v(1384.3, 1803.4) * mm, "end": v(1384.3, 2590.8) * mm});
            skLineSegment(sketch, "E46.bottom", {"start": v(1384.3, 1803.4) * mm, "end": v(1447.8, 1803.4) * mm});
            skLineSegment(sketch, "E46.top", {"start": v(1384.3, 1784.35) * mm, "end": v(1447.8, 1784.35) * mm});
            skLineSegment(sketch, "E46.left", {"start": v(1384.3, 1803.4) * mm, "end": v(1384.3, 1784.35) * mm});
            skLineSegment(sketch, "E46.right", {"start": v(1447.8, 1803.4) * mm, "end": v(1447.8, 1784.35) * mm});
            skLineSegment(sketch, "E47.bottom", {"start": v(2971.8, 1803.4) * mm, "end": v(3035.3, 1803.4) * mm});
            skLineSegment(sketch, "E47.top", {"start": v(2971.8, 1784.35) * mm, "end": v(3035.3, 1784.35) * mm});
            skLineSegment(sketch, "E47.left", {"start": v(2971.8, 1803.4) * mm, "end": v(2971.8, 1784.35) * mm});
            skLineSegment(sketch, "E47.right", {"start": v(3035.3, 1803.4) * mm, "end": v(3035.3, 1784.35) * mm});
            skSolve(sketch);
        }
        {
            var Q0;
            Q0=qSketchRegion(id+"F28",true);
            extrude(context, id + "F29", {"entities" : qUnion([Q0]), "operationType" : NewBodyOperationType.ADD, "depth" : 1447.8 * mm});
        }
        {
            var Q0;
            Q0=makeQuery(id+"F29.opExtrude","CAP_FACE",FACE,{"disambiguationData":[OSD([sQuery(id+"F28.wireOp",EDGE,"E45.top"),sQuery(id+"F28.wireOp",EDGE,"E45.left"),sQuery(id+"F28.wireOp",EDGE,"E45.right"),sQuery(id+"F28.wireOp",EDGE,"E46.bottom"),sQuery(id+"F28.wireOp",EDGE,"E46.top"),sQuery(id+"F28.wireOp",EDGE,"E46.left"),sQuery(id+"F28.wireOp",EDGE,"E46.right")])],"isStart":false});
            var sketch = newSketch(context, id + "F30", { "sketchPlane" : qUnion([Q0])});
            skLineSegment(sketch, "E48.bottom", {"start": v(1384.3, 2590.8) * mm, "end": v(1403.35, 2590.8) * mm});
            skLineSegment(sketch, "E48.top", {"start": v(1384.3, 1803.4) * mm, "end": v(1403.35, 1803.4) * mm});
            skLineSegment(sketch, "E48.left", {"start": v(1384.3, 2590.8) * mm, "end": v(1384.3, 1803.4) * mm});
            skLineSegment(sketch, "E48.right", {"start": v(1403.35, 2590.8) * mm, "end": v(1403.35, 1803.4) * mm});
            skSolve(sketch);
        }
        {
            var Q0;
            Q0=qSketchRegion(id+"F30",true);
            extrude(context, id + "F31", {"entities" : qUnion([Q0]), "operationType" : NewBodyOperationType.REMOVE, "oppositeDirection" : true, "depth" : 19.05 * mm});
        }
        {
            var Q0;
            Q0=makeQuery(id+"F31.boolean.opBoolean","COPY",FACE,{"derivedFrom":makeQuery(id+"F31.opExtrude","CAP_FACE",FACE,{"disambiguationData":[OSD([sQuery(id+"F30.wireOp",EDGE,"E48.bottom"),sQuery(id+"F30.wireOp",EDGE,"E48.top"),sQuery(id+"F30.wireOp",EDGE,"E48.left"),sQuery(id+"F30.wireOp",EDGE,"E48.right")])],"isStart":false})});
            var sketch = newSketch(context, id + "F32", { "sketchPlane" : qUnion([Q0])});
            skLineSegment(sketch, "E49.bottom", {"start": v(3035.3, 2590.8) * mm, "end": v(469.9, 2590.8) * mm});
            skLineSegment(sketch, "E49.top", {"start": v(3035.3, 1803.4) * mm, "end": v(469.9, 1803.4) * mm});
            skLineSegment(sketch, "E49.left", {"start": v(3035.3, 2590.8) * mm, "end": v(3035.3, 1803.4) * mm});
            skLineSegment(sketch, "E49.right", {"start": v(469.9, 2590.8) * mm, "end": v(469.9, 1803.4) * mm});
            skSolve(sketch);
        }
        {
            var Q0;
            Q0=qSketchRegion(id+"F32",true);
            extrude(context, id + "F33", {"entities" : qUnion([Q0]), "operationType" : NewBodyOperationType.ADD, "depth" : 19.05 * mm});
        }
        {
            var Q0;
            Q0=makeQuery(id+"F33.boolean.opBoolean","SPLIT",FACE,{"disambiguationData":[TD([makeQuery(id+"F29.opExtrude","SWEPT_FACE",FACE,{"disambiguationData":[OSD([sQuery(id+"F28.wireOp",EDGE,"E45.left")])]})])],"derivedFrom":makeQuery(id+"F31.boolean.opBoolean","MERGE",FACE,{"derivedFrom":[makeQuery(id+"F5.opExtrude","CAP_FACE",FACE,{"disambiguationData":[OSD([sQuery(id+"F4.wireOp",EDGE,"E2.bottom"),sQuery(id+"F4.wireOp",EDGE,"E2.top"),sQuery(id+"F4.wireOp",EDGE,"E2.left"),sQuery(id+"F4.wireOp",EDGE,"E2.right")])],"isStart":true}),makeQuery(id+"F31.opExtrude","SWEPT_FACE",FACE,{"disambiguationData":[OSD([sQuery(id+"F30.wireOp",EDGE,"E48.bottom")])]})]})});
            var sketch = newSketch(context, id + "F34", { "sketchPlane" : qUnion([Q0])});
            skLineSegment(sketch, "E50.bottom", {"start": v(1403.35, 406.4) * mm, "end": v(3035.3, 406.4) * mm});
            skLineSegment(sketch, "E50.top", {"start": v(1403.35, 425.45) * mm, "end": v(3035.3, 425.45) * mm});
            skLineSegment(sketch, "E50.left", {"start": v(1403.35, 406.4) * mm, "end": v(1403.35, 425.45) * mm});
            skLineSegment(sketch, "E50.right", {"start": v(3035.3, 406.4) * mm, "end": v(3035.3, 425.45) * mm});
            skSolve(sketch);
        }
        {
            var Q0;
            Q0=qSketchRegion(id+"F34",true);
            extrude(context, id + "F35", {"entities" : qUnion([Q0]), "operationType" : NewBodyOperationType.ADD, "depth" : 787.4 * mm});
        }
        {
            var Q0;
            {var subQ0=sQuery(id+"F17.wireOp",EDGE,"E17.right");var subQ1=sQuery(id+"F17.wireOp",EDGE,"E17.bottom");var subQ2=makeQuery(id+"F17.imprint","INTERSECT",VERTEX,{"derivedFrom":[subQ1,subQ0]});Q0=makeQuery(id+"F17.imprint","IMPRINT",FACE,{"disambiguationData":[TD([[makeQuery(id+"F17.imprint","IMPRINT",EDGE,{"disambiguationData":[TD([[subQ2,1.0]])],"derivedFrom":subQ1}),-1.0]])]});}
            var sketch = newSketch(context, id + "F36", { "sketchPlane" : qUnion([Q0])});
            skLineSegment(sketch, "E51.bottom", {"start": v(1384.3, 2590.8) * mm, "end": v(165.1, 2590.8) * mm});
            skLineSegment(sketch, "E51.top", {"start": v(1384.3, 323.85) * mm, "end": v(165.1, 323.85) * mm});
            skLineSegment(sketch, "E51.left", {"start": v(1384.3, 2590.8) * mm, "end": v(1384.3, 323.85) * mm});
            skLineSegment(sketch, "E51.right", {"start": v(165.1, 2590.8) * mm, "end": v(165.1, 323.85) * mm});
            skSolve(sketch);
        }
        {
            var Q0;
            Q0 = qSketchRegion(id + "F36", true);
            extrude(context, id + "F37", {"entities" : qUnion([Q0]), "operationType" : NewBodyOperationType.REMOVE, "endBound" : BoundingType.THROUGH_ALL, "depth" : 25.4 * mm});
        }
        {
            var Q0;
            Q0=makeQuery(id+"F37.boolean.opBoolean","MERGE",FACE,{"derivedFrom":[makeQuery(id+"F13.opExtrude","CAP_FACE",FACE,{"disambiguationData":[OSD([sQuery(id+"F12.wireOp",EDGE,"E8.bottom"),sQuery(id+"F12.wireOp",EDGE,"E8.top"),sQuery(id+"F12.wireOp",EDGE,"E8.left"),sQuery(id+"F12.wireOp",EDGE,"E8.right")])],"isStart":true}),makeQuery(id+"F37.opExtrude","CAP_FACE",FACE,{"disambiguationData":[OSD([sQuery(id+"F36.wireOp",EDGE,"E51.bottom"),sQuery(id+"F36.wireOp",EDGE,"E51.top"),sQuery(id+"F36.wireOp",EDGE,"E51.left"),sQuery(id+"F36.wireOp",EDGE,"E51.right")])],"isStart":true})]});
            var sketch = newSketch(context, id + "F38", { "sketchPlane" : qUnion([Q0])});
            skLineSegment(sketch, "E52.top", {"start": v(165.1, 1784.35) * mm, "end": v(228.6, 1784.35) * mm});
            skLineSegment(sketch, "E52.left", {"start": v(165.1, 1803.4) * mm, "end": v(165.1, 1784.35) * mm});
            skLineSegment(sketch, "E52.right", {"start": v(228.6, 1803.4) * mm, "end": v(228.6, 1784.35) * mm});
            skLineSegment(sketch, "E53", {"start": v(165.1, 1803.4) * mm, "end": v(228.6, 1803.4) * mm});
            skLineSegment(sketch, "E54.bottom", {"start": v(1206.5, 2590.8) * mm, "end": v(1187.45, 2590.8) * mm});
            skLineSegment(sketch, "E54.top", {"start": v(1206.5, 1803.4) * mm, "end": v(1187.45, 1803.4) * mm});
            skLineSegment(sketch, "E54.left", {"start": v(1206.5, 2590.8) * mm, "end": v(1206.5, 1803.4) * mm});
            skLineSegment(sketch, "E54.right", {"start": v(1187.45, 2590.8) * mm, "end": v(1187.45, 1803.4) * mm});
            skLineSegment(sketch, "E55.bottom", {"start": v(1206.5, 1803.4) * mm, "end": v(1143, 1803.4) * mm});
            skLineSegment(sketch, "E55.top", {"start": v(1206.5, 1784.35) * mm, "end": v(1143, 1784.35) * mm});
            skLineSegment(sketch, "E55.left", {"start": v(1206.5, 1803.4) * mm, "end": v(1206.5, 1784.35) * mm});
            skLineSegment(sketch, "E55.right", {"start": v(1143, 1803.4) * mm, "end": v(1143, 1784.35) * mm});
            skSolve(sketch);
        }
        {
            var Q0;
            Q0 = qSketchRegion(id + "F38", true);
            extrude(context, id + "F39", {"entities" : qUnion([Q0]), "operationType" : NewBodyOperationType.ADD, "depth" : 1771.65 * mm});
        }
        {
            var Q0;
            Q0=makeQuery(id+"F39.opExtrude","CAP_FACE",FACE,{"disambiguationData":[OSD([sQuery(id+"F38.wireOp",EDGE,"E52.bottom"),sQuery(id+"F38.wireOp",EDGE,"E52.top"),sQuery(id+"F38.wireOp",EDGE,"E52.left"),sQuery(id+"F38.wireOp",EDGE,"E52.right"),sQuery(id+"F38.wireOp",EDGE,"P4kx2W43-oSlM-iuyH-3Pe2-vS2qbAO8ddNj.top"),sQuery(id+"F38.wireOp",EDGE,"P4kx2W43-oSlM-iuyH-3Pe2-vS2qbAO8ddNj.left"),sQuery(id+"F38.wireOp",EDGE,"P4kx2W43-oSlM-iuyH-3Pe2-vS2qbAO8ddNj.right")])],"isStart":false});
            var sketch = newSketch(context, id + "F40", { "sketchPlane" : qUnion([Q0])});
            skLineSegment(sketch, "E56.bottom", {"start": v(1187.45, 2590.8) * mm, "end": v(1206.5, 2590.8) * mm});
            skLineSegment(sketch, "E56.top", {"start": v(1187.45, 1803.4) * mm, "end": v(1206.5, 1803.4) * mm});
            skLineSegment(sketch, "E56.left", {"start": v(1187.45, 2590.8) * mm, "end": v(1187.45, 1803.4) * mm});
            skLineSegment(sketch, "E56.right", {"start": v(1206.5, 2590.8) * mm, "end": v(1206.5, 1803.4) * mm});
            skSolve(sketch);
        }
        {
            var Q0;
            Q0 = qSketchRegion(id + "F40", true);
            extrude(context, id + "F41", {"entities" : qUnion([Q0]), "operationType" : NewBodyOperationType.REMOVE, "oppositeDirection" : true, "depth" : 19.05 * mm});
        }
        {
            var Q0;
            Q0=makeQuery(id+"F41.boolean.opBoolean","COPY",FACE,{"derivedFrom":makeQuery(id+"F41.opExtrude","CAP_FACE",FACE,{"disambiguationData":[OSD([sQuery(id+"F40.wireOp",EDGE,"E56.bottom"),sQuery(id+"F40.wireOp",EDGE,"E56.top"),sQuery(id+"F40.wireOp",EDGE,"E56.left"),sQuery(id+"F40.wireOp",EDGE,"E56.right")])],"isStart":false})});
            var sketch = newSketch(context, id + "F42", { "sketchPlane" : qUnion([Q0])});
            skLineSegment(sketch, "E57.bottom", {"start": v(3035.3, 1803.4) * mm, "end": v(165.1, 1803.4) * mm});
            skLineSegment(sketch, "E57.top", {"start": v(3035.3, 2590.8) * mm, "end": v(165.1, 2590.8) * mm});
            skLineSegment(sketch, "E57.left", {"start": v(3035.3, 1803.4) * mm, "end": v(3035.3, 2590.8) * mm});
            skLineSegment(sketch, "E57.right", {"start": v(165.1, 1803.4) * mm, "end": v(165.1, 2590.8) * mm});
            skSolve(sketch);
        }
        {
            var Q0;
            Q0 = qSketchRegion(id + "F42", true);
            extrude(context, id + "F43", {"entities" : qUnion([Q0]), "operationType" : NewBodyOperationType.ADD, "depth" : 19.05 * mm});
        }
        {
            var Q0;
            {var subQ11=makeQuery(id+"F19.opExtrude","SWEPT_FACE",FACE,{"disambiguationData":[OSD([sQuery(id+"F18.wireOp",EDGE,"E21.top")])]});var subQ14=sQuery(id+"F36.wireOp",EDGE,"E51.bottom");var subQ21=makeQuery(id+"F31.boolean.opBoolean","MERGE",FACE,{"derivedFrom":[makeQuery(id+"F5.opExtrude","CAP_FACE",FACE,{"disambiguationData":[OSD([sQuery(id+"F4.wireOp",EDGE,"E2.bottom"),sQuery(id+"F4.wireOp",EDGE,"E2.top"),sQuery(id+"F4.wireOp",EDGE,"E2.left"),sQuery(id+"F4.wireOp",EDGE,"E2.right")])],"isStart":true}),makeQuery(id+"F31.opExtrude","SWEPT_FACE",FACE,{"disambiguationData":[OSD([sQuery(id+"F30.wireOp",EDGE,"E48.bottom")])]})]});Q0=makeQuery(id+"F43.boolean.opBoolean","SPLIT",FACE,{"disambiguationData":[TD([subQ11])],"derivedFrom":makeQuery(id+"F41.boolean.opBoolean","MERGE",FACE,{"derivedFrom":[makeQuery(id+"F37.boolean.opBoolean","MERGE",FACE,{"derivedFrom":[makeQuery(id+"F33.boolean.opBoolean","SPLIT",FACE,{"disambiguationData":[TD([makeQuery(id+"F19.opExtrude","SWEPT_FACE",FACE,{"disambiguationData":[OSD([sQuery(id+"F18.wireOp",EDGE,"E18.bottom")])]})])],"derivedFrom":subQ21}),makeQuery(id+"F33.boolean.opBoolean","SPLIT",FACE,{"disambiguationData":[TD([makeQuery(id+"F10.boolean.opBoolean","COPY",FACE,{"derivedFrom":makeQuery(id+"F10.opExtrude","SWEPT_FACE",FACE,{"disambiguationData":[OSD([sQuery(id+"F9.wireOp",EDGE,"E5")])]})})])],"derivedFrom":subQ21}),makeQuery(id+"F37.opExtrude","SWEPT_FACE",FACE,{"disambiguationData":[OSD([subQ14])]})]}),makeQuery(id+"F41.opExtrude","SWEPT_FACE",FACE,{"disambiguationData":[OSD([sQuery(id+"F40.wireOp",EDGE,"E56.bottom")])]})]})});}
            var sketch = newSketch(context, id + "F44", { "sketchPlane" : qUnion([Q0])});
            skLineSegment(sketch, "E58.bottom", {"start": v(1384.3, 1752.6) * mm, "end": v(1403.35, 1752.6) * mm});
            skLineSegment(sketch, "E58.top", {"start": v(1384.3, 1428.75) * mm, "end": v(1403.35, 1428.75) * mm});
            skLineSegment(sketch, "E58.left", {"start": v(1384.3, 1428.75) * mm, "end": v(1384.3, 1752.6) * mm});
            skLineSegment(sketch, "E58.right", {"start": v(1403.35, 1428.75) * mm, "end": v(1403.35, 1752.6) * mm});
            skSolve(sketch);
        }
        {
            var Q0;
            Q0 = qSketchRegion(id + "F44", true);
            extrude(context, id + "F45", {"entities" : qUnion([Q0]), "operationType" : NewBodyOperationType.ADD, "depth" : 787.4 * mm});
        }
        {
            var Q0;
            {var subQ0=sQuery(id+"F28.wireOp",EDGE,"E46.right");var subQ1=sQuery(id+"F28.wireOp",EDGE,"E47.left");var subQ2=sQuery(id+"F28.wireOp",EDGE,"E47.top");var subQ3=sQuery(id+"F32.wireOp",EDGE,"E49.top");var subQ4=sQuery(id+"F28.wireOp",EDGE,"E46.left");var subQ5=sQuery(id+"F28.wireOp",EDGE,"E45.right");var subQ6=sQuery(id+"F28.wireOp",EDGE,"E46.top");Q0=makeQuery(id+"F37.boolean.opBoolean","SPLIT",FACE,{"disambiguationData":[TD([makeQuery(id+"F29.opExtrude","SWEPT_FACE",FACE,{"disambiguationData":[OSD([subQ6])]})])],"derivedFrom":makeQuery(id+"F33.boolean.opBoolean","MERGE",FACE,{"derivedFrom":[makeQuery(id+"F25.boolean.opBoolean","MERGE",FACE,{"derivedFrom":[makeQuery(id+"F19.opExtrude","SWEPT_FACE",FACE,{"disambiguationData":[OSD([sQuery(id+"F18.wireOp",EDGE,"E21.top")])]}),makeQuery(id+"F25.opExtrude","SWEPT_FACE",FACE,{"disambiguationData":[OSD([sQuery(id+"F24.wireOp",EDGE,"E39.bottom")])]})]}),makeQuery(id+"F29.opExtrude","CAP_FACE",FACE,{"disambiguationData":[OSD([sQuery(id+"F28.wireOp",EDGE,"E47.bottom"),subQ2,subQ1,sQuery(id+"F28.wireOp",EDGE,"E47.right")])],"isStart":false}),makeQuery(id+"F29.opExtrude","CAP_FACE",FACE,{"disambiguationData":[OSD([sQuery(id+"F28.wireOp",EDGE,"E45.top"),sQuery(id+"F28.wireOp",EDGE,"E45.left"),subQ5,sQuery(id+"F28.wireOp",EDGE,"E46.bottom"),subQ6,subQ4,subQ0])],"isStart":false}),makeQuery(id+"F33.opExtrude","CAP_FACE",FACE,{"disambiguationData":[OSD([sQuery(id+"F32.wireOp",EDGE,"E49.bottom"),subQ3,sQuery(id+"F32.wireOp",EDGE,"E49.left"),sQuery(id+"F32.wireOp",EDGE,"E49.right")])],"isStart":false})]})});}
            var sketch = newSketch(context, id + "F46", { "sketchPlane" : qUnion([Q0])});
            skLineSegment(sketch, "E59.bottom", {"start": v(1384.3, 1784.35) * mm, "end": v(1447.8, 1784.35) * mm});
            skLineSegment(sketch, "E59.top", {"start": v(1384.3, 1803.4) * mm, "end": v(1447.8, 1803.4) * mm});
            skLineSegment(sketch, "E59.left", {"start": v(1384.3, 1784.35) * mm, "end": v(1384.3, 1803.4) * mm});
            skLineSegment(sketch, "E59.right", {"start": v(1447.8, 1784.35) * mm, "end": v(1447.8, 1803.4) * mm});
            skLineSegment(sketch, "E60.bottom", {"start": v(2971.8, 1803.4) * mm, "end": v(3035.3, 1803.4) * mm});
            skLineSegment(sketch, "E60.top", {"start": v(2971.8, 1784.35) * mm, "end": v(3035.3, 1784.35) * mm});
            skLineSegment(sketch, "E60.left", {"start": v(2971.8, 1803.4) * mm, "end": v(2971.8, 1784.35) * mm});
            skLineSegment(sketch, "E60.right", {"start": v(3035.3, 1803.4) * mm, "end": v(3035.3, 1784.35) * mm});
            skSolve(sketch);
        }
        {
            var Q0;
            Q0 = qSketchRegion(id + "F46", true);
            var Q1;
            Q1=makeQuery(id+"F43.boolean.opBoolean","MERGE",FACE,{"derivedFrom":[makeQuery(id+"F39.opExtrude","CAP_FACE",FACE,{"disambiguationData":[OSD([sQuery(id+"F38.wireOp",EDGE,"Gv2CieVk-ht9b-cRYq-0Ijf-CqdY1RLyHL7K.bottom"),sQuery(id+"F38.wireOp",EDGE,"Gv2CieVk-ht9b-cRYq-0Ijf-CqdY1RLyHL7K.top"),sQuery(id+"F38.wireOp",EDGE,"Gv2CieVk-ht9b-cRYq-0Ijf-CqdY1RLyHL7K.left"),sQuery(id+"F38.wireOp",EDGE,"Gv2CieVk-ht9b-cRYq-0Ijf-CqdY1RLyHL7K.right")])],"isStart":false}),makeQuery(id+"F39.opExtrude","CAP_FACE",FACE,{"disambiguationData":[OSD([sQuery(id+"F38.wireOp",EDGE,"E52.bottom"),sQuery(id+"F38.wireOp",EDGE,"E52.top"),sQuery(id+"F38.wireOp",EDGE,"E52.left"),sQuery(id+"F38.wireOp",EDGE,"E52.right"),sQuery(id+"F38.wireOp",EDGE,"P4kx2W43-oSlM-iuyH-3Pe2-vS2qbAO8ddNj.top"),sQuery(id+"F38.wireOp",EDGE,"P4kx2W43-oSlM-iuyH-3Pe2-vS2qbAO8ddNj.left"),sQuery(id+"F38.wireOp",EDGE,"P4kx2W43-oSlM-iuyH-3Pe2-vS2qbAO8ddNj.right")])],"isStart":false}),makeQuery(id+"F43.opExtrude","CAP_FACE",FACE,{"disambiguationData":[OSD([sQuery(id+"F42.wireOp",EDGE,"E57.bottom"),sQuery(id+"F42.wireOp",EDGE,"E57.top"),sQuery(id+"F42.wireOp",EDGE,"E57.left"),sQuery(id+"F42.wireOp",EDGE,"E57.right")])],"isStart":false})]});
            extrude(context, id + "F47", {"entities" : qUnion([Q0]), "operationType" : NewBodyOperationType.ADD, "endBound" : BoundingType.UP_TO_SURFACE, "endBoundEntityFace" : qUnion([Q1]), "depth" : 25.4 * mm});
        }
        {
            var Q0;
            {var subQ0=sQuery(id+"F38.wireOp",EDGE,"E55.left");var subQ1=sQuery(id+"F38.wireOp",EDGE,"E54.left");var subQ3=sQuery(id+"F44.wireOp",EDGE,"E58.left");var subQ6=makeQuery(id+"F39.opExtrude","SWEPT_FACE",FACE,{"disambiguationData":[OSD([subQ1,subQ0])]});var subQ10=sQuery(id+"F42.wireOp",EDGE,"E57.bottom");Q0=makeQuery(id+"F47.boolean.opBoolean","SPLIT",FACE,{"disambiguationData":[TD([makeQuery(id+"F45.opExtrude","SWEPT_FACE",FACE,{"disambiguationData":[OSD([subQ3])]})])],"derivedFrom":makeQuery(id+"F45.boolean.opBoolean","MERGE",FACE,{"derivedFrom":[makeQuery(id+"F43.boolean.opBoolean","SPLIT",FACE,{"disambiguationData":[TD([subQ6])],"derivedFrom":makeQuery(id+"F43.opExtrude","SWEPT_FACE",FACE,{"disambiguationData":[OSD([subQ10])]})}),makeQuery(id+"F45.opExtrude","CAP_FACE",FACE,{"disambiguationData":[OSD([sQuery(id+"F44.wireOp",EDGE,"E58.bottom"),sQuery(id+"F44.wireOp",EDGE,"E58.top"),subQ3,sQuery(id+"F44.wireOp",EDGE,"E58.right")])],"isStart":false})]})});}
            var sketch = newSketch(context, id + "F48", { "sketchPlane" : qUnion([Q0])});
            skLineSegment(sketch, "E61.bottom", {"start": v(1206.5, 406.4) * mm, "end": v(1384.3, 406.4) * mm});
            skLineSegment(sketch, "E61.top", {"start": v(1206.5, 425.45) * mm, "end": v(1384.3, 425.45) * mm});
            skLineSegment(sketch, "E61.left", {"start": v(1206.5, 406.4) * mm, "end": v(1206.5, 425.45) * mm});
            skLineSegment(sketch, "E61.right", {"start": v(1384.3, 406.4) * mm, "end": v(1384.3, 425.45) * mm});
            skLineSegment(sketch, "E62.bottom", {"start": v(1206.5, 781.05) * mm, "end": v(1384.3, 781.05) * mm});
            skLineSegment(sketch, "E62.top", {"start": v(1206.5, 800.1) * mm, "end": v(1384.3, 800.1) * mm});
            skLineSegment(sketch, "E62.left", {"start": v(1206.5, 781.05) * mm, "end": v(1206.5, 800.1) * mm});
            skLineSegment(sketch, "E62.right", {"start": v(1384.3, 781.05) * mm, "end": v(1384.3, 800.1) * mm});
            skLineSegment(sketch, "E63.bottom", {"start": v(1206.5, 1104.9) * mm, "end": v(1384.3, 1104.9) * mm});
            skLineSegment(sketch, "E63.top", {"start": v(1206.5, 1123.95) * mm, "end": v(1384.3, 1123.95) * mm});
            skLineSegment(sketch, "E63.left", {"start": v(1206.5, 1104.9) * mm, "end": v(1206.5, 1123.95) * mm});
            skLineSegment(sketch, "E63.right", {"start": v(1384.3, 1104.9) * mm, "end": v(1384.3, 1123.95) * mm});
            skLineSegment(sketch, "E64.bottom", {"start": v(1206.5, 1428.75) * mm, "end": v(1384.3, 1428.75) * mm});
            skLineSegment(sketch, "E64.top", {"start": v(1206.5, 1447.8) * mm, "end": v(1384.3, 1447.8) * mm});
            skLineSegment(sketch, "E64.left", {"start": v(1206.5, 1428.75) * mm, "end": v(1206.5, 1447.8) * mm});
            skLineSegment(sketch, "E64.right", {"start": v(1384.3, 1428.75) * mm, "end": v(1384.3, 1447.8) * mm});
            skSolve(sketch);
        }
        {
            var Q0;
            Q0 = qSketchRegion(id + "F48", true);
            extrude(context, id + "F49", {"entities" : qUnion([Q0]), "operationType" : NewBodyOperationType.ADD, "oppositeDirection" : true, "depth" : 787.4 * mm});
        }
        {
            var Q0;
            {var subQ6=makeQuery(id+"F19.opExtrude","SWEPT_FACE",FACE,{"disambiguationData":[OSD([sQuery(id+"F18.wireOp",EDGE,"E18.bottom")])]});var subQ32=makeQuery(id+"F19.opExtrude","SWEPT_FACE",FACE,{"disambiguationData":[OSD([sQuery(id+"F18.wireOp",EDGE,"E20.top")])]});var subQ33=makeQuery(id+"F19.opExtrude","SWEPT_FACE",FACE,{"disambiguationData":[OSD([sQuery(id+"F18.wireOp",EDGE,"E18.top")])]});var subQ37=makeQuery(id+"F10.boolean.opBoolean","COPY",FACE,{"derivedFrom":makeQuery(id+"F10.opExtrude","SWEPT_FACE",FACE,{"disambiguationData":[OSD([sQuery(id+"F9.wireOp",EDGE,"E5")])]})});var subQ39=makeQuery(id+"F19.opExtrude","SWEPT_FACE",FACE,{"disambiguationData":[OSD([sQuery(id+"F18.wireOp",EDGE,"E19.top")])]});var subQ48=makeQuery(id+"F19.opExtrude","SWEPT_FACE",FACE,{"disambiguationData":[OSD([sQuery(id+"F18.wireOp",EDGE,"E21.top")])]});var subQ51=makeQuery(id+"F19.opExtrude","SWEPT_FACE",FACE,{"disambiguationData":[OSD([sQuery(id+"F18.wireOp",EDGE,"E22.top")])]});var subQ60=sQuery(id+"F36.wireOp",EDGE,"E51.right");var subQ62=makeQuery(id+"F1.opExtrude","CAP_FACE",FACE,{"disambiguationData":[OSD([sQuery(id+"F0.wireOp",EDGE,"E0.bottom"),sQuery(id+"F0.wireOp",EDGE,"E0.top"),sQuery(id+"F0.wireOp",EDGE,"E0.left"),sQuery(id+"F0.wireOp",EDGE,"E0.right")])],"isStart":false});Q0=makeQuery(id+"F43.boolean.opBoolean","SPLIT",FACE,{"disambiguationData":[TD([subQ37])],"derivedFrom":makeQuery(id+"F37.boolean.opBoolean","MERGE",FACE,{"derivedFrom":[makeQuery(id+"F25.boolean.opBoolean","SPLIT",FACE,{"disambiguationData":[TD([subQ37])],"derivedFrom":subQ62}),makeQuery(id+"F25.boolean.opBoolean","SPLIT",FACE,{"disambiguationData":[TD([subQ6])],"derivedFrom":subQ62}),makeQuery(id+"F25.boolean.opBoolean","SPLIT",FACE,{"disambiguationData":[TD([subQ33])],"derivedFrom":subQ62}),makeQuery(id+"F25.boolean.opBoolean","SPLIT",FACE,{"disambiguationData":[TD([subQ39])],"derivedFrom":subQ62}),makeQuery(id+"F25.boolean.opBoolean","SPLIT",FACE,{"disambiguationData":[TD([subQ32])],"derivedFrom":subQ62}),makeQuery(id+"F25.boolean.opBoolean","SPLIT",FACE,{"disambiguationData":[TD([subQ48])],"derivedFrom":subQ62}),makeQuery(id+"F25.boolean.opBoolean","SPLIT",FACE,{"disambiguationData":[TD([subQ51])],"derivedFrom":subQ62}),makeQuery(id+"F37.opExtrude","SWEPT_FACE",FACE,{"disambiguationData":[OSD([subQ60])]})]})});}
            var sketch = newSketch(context, id + "F50", { "sketchPlane" : qUnion([Q0])});
            skLineSegment(sketch, "E65.bottom", {"start": v(323.85, 425.45) * mm, "end": v(730.25, 425.45) * mm});
            skLineSegment(sketch, "E65.top", {"start": v(323.85, 406.4) * mm, "end": v(730.25, 406.4) * mm});
            skLineSegment(sketch, "E65.left", {"start": v(323.85, 425.45) * mm, "end": v(323.85, 406.4) * mm});
            skLineSegment(sketch, "E65.right", {"start": v(730.25, 425.45) * mm, "end": v(730.25, 406.4) * mm});
            skLineSegment(sketch, "E66.bottom", {"start": v(323.85, 800.1) * mm, "end": v(730.25, 800.1) * mm});
            skLineSegment(sketch, "E66.top", {"start": v(323.85, 781.05) * mm, "end": v(730.25, 781.05) * mm});
            skLineSegment(sketch, "E66.left", {"start": v(323.85, 800.1) * mm, "end": v(323.85, 781.05) * mm});
            skLineSegment(sketch, "E66.right", {"start": v(730.25, 800.1) * mm, "end": v(730.25, 781.05) * mm});
            skLineSegment(sketch, "E67.bottom", {"start": v(323.85, 1123.95) * mm, "end": v(730.25, 1123.95) * mm});
            skLineSegment(sketch, "E67.top", {"start": v(323.85, 1104.9) * mm, "end": v(730.25, 1104.9) * mm});
            skLineSegment(sketch, "E67.left", {"start": v(323.85, 1123.95) * mm, "end": v(323.85, 1104.9) * mm});
            skLineSegment(sketch, "E67.right", {"start": v(730.25, 1123.95) * mm, "end": v(730.25, 1104.9) * mm});
            skLineSegment(sketch, "E68.bottom", {"start": v(323.85, 1447.8) * mm, "end": v(730.25, 1447.8) * mm});
            skLineSegment(sketch, "E68.top", {"start": v(323.85, 1428.75) * mm, "end": v(730.25, 1428.75) * mm});
            skLineSegment(sketch, "E68.left", {"start": v(323.85, 1447.8) * mm, "end": v(323.85, 1428.75) * mm});
            skLineSegment(sketch, "E68.right", {"start": v(730.25, 1447.8) * mm, "end": v(730.25, 1428.75) * mm});
            skLineSegment(sketch, "E69.bottom", {"start": v(323.85, 1771.65) * mm, "end": v(730.25, 1771.65) * mm});
            skLineSegment(sketch, "E69.top", {"start": v(323.85, 1752.6) * mm, "end": v(730.25, 1752.6) * mm});
            skLineSegment(sketch, "E69.left", {"start": v(323.85, 1771.65) * mm, "end": v(323.85, 1752.6) * mm});
            skLineSegment(sketch, "E69.right", {"start": v(730.25, 1771.65) * mm, "end": v(730.25, 1752.6) * mm});
            skLineSegment(sketch, "E70.bottom", {"start": v(323.85, 2095.5) * mm, "end": v(730.25, 2095.5) * mm});
            skLineSegment(sketch, "E70.top", {"start": v(323.85, 2076.45) * mm, "end": v(730.25, 2076.45) * mm});
            skLineSegment(sketch, "E70.left", {"start": v(323.85, 2095.5) * mm, "end": v(323.85, 2076.45) * mm});
            skLineSegment(sketch, "E70.right", {"start": v(730.25, 2095.5) * mm, "end": v(730.25, 2076.45) * mm});
            skSolve(sketch);
        }
        {
            var Q0;
            Q0 = qSketchRegion(id + "F50", true);
            extrude(context, id + "F51", {"entities" : qUnion([Q0]), "operationType" : NewBodyOperationType.ADD, "depth" : 304.8 * mm});
        }
        {
            var Q0;
            Q0=makeQuery(id+"F37.boolean.opBoolean","MERGE",FACE,{"derivedFrom":[makeQuery(id+"F13.opExtrude","CAP_FACE",FACE,{"disambiguationData":[OSD([sQuery(id+"F12.wireOp",EDGE,"E8.bottom"),sQuery(id+"F12.wireOp",EDGE,"E8.top"),sQuery(id+"F12.wireOp",EDGE,"E8.left"),sQuery(id+"F12.wireOp",EDGE,"E8.right")])],"isStart":true}),makeQuery(id+"F37.opExtrude","CAP_FACE",FACE,{"disambiguationData":[OSD([sQuery(id+"F36.wireOp",EDGE,"E51.bottom"),sQuery(id+"F36.wireOp",EDGE,"E51.top"),sQuery(id+"F36.wireOp",EDGE,"E51.left"),sQuery(id+"F36.wireOp",EDGE,"E51.right")])],"isStart":true})]});
            var sketch = newSketch(context, id + "F52", { "sketchPlane" : qUnion([Q0])});
            skLineSegment(sketch, "E71.bottom", {"start": v(469.9, 323.85) * mm, "end": v(488.95, 323.85) * mm});
            skLineSegment(sketch, "E71.top", {"start": v(469.9, 387.35) * mm, "end": v(488.95, 387.35) * mm});
            skLineSegment(sketch, "E71.left", {"start": v(469.9, 323.85) * mm, "end": v(469.9, 387.35) * mm});
            skLineSegment(sketch, "E71.right", {"start": v(488.95, 323.85) * mm, "end": v(488.95, 387.35) * mm});
            skLineSegment(sketch, "E72.bottom", {"start": v(469.9, 685.8) * mm, "end": v(488.95, 685.8) * mm});
            skLineSegment(sketch, "E72.top", {"start": v(469.9, 749.3) * mm, "end": v(488.95, 749.3) * mm});
            skLineSegment(sketch, "E72.left", {"start": v(469.9, 685.8) * mm, "end": v(469.9, 749.3) * mm});
            skLineSegment(sketch, "E72.right", {"start": v(488.95, 685.8) * mm, "end": v(488.95, 749.3) * mm});
            skLineSegment(sketch, "E73.bottom", {"start": v(165.1, 730.25) * mm, "end": v(228.6, 730.25) * mm});
            skLineSegment(sketch, "E73.top", {"start": v(165.1, 749.3) * mm, "end": v(228.6, 749.3) * mm});
            skLineSegment(sketch, "E73.left", {"start": v(165.1, 730.25) * mm, "end": v(165.1, 749.3) * mm});
            skLineSegment(sketch, "E73.right", {"start": v(228.6, 730.25) * mm, "end": v(228.6, 749.3) * mm});
            skLineSegment(sketch, "E74.bottom", {"start": v(469.9, 749.3) * mm, "end": v(406.4, 749.3) * mm});
            skLineSegment(sketch, "E74.top", {"start": v(469.9, 730.25) * mm, "end": v(406.4, 730.25) * mm});
            skLineSegment(sketch, "E74.left", {"start": v(469.9, 749.3) * mm, "end": v(469.9, 730.25) * mm});
            skLineSegment(sketch, "E74.right", {"start": v(406.4, 749.3) * mm, "end": v(406.4, 730.25) * mm});
            skSolve(sketch);
        }
        {
            var Q0;
            Q0 = qSketchRegion(id + "F52", true);
            var Q1;
            Q1=makeQuery(id+"F51.boolean.opBoolean","MERGE",FACE,{"derivedFrom":[makeQuery(id+"F25.boolean.opBoolean","MERGE",FACE,{"derivedFrom":[makeQuery(id+"F23.boolean.opBoolean","MERGE",FACE,{"derivedFrom":[makeQuery(id+"F19.opExtrude","SWEPT_FACE",FACE,{"disambiguationData":[OSD([sQuery(id+"F18.wireOp",EDGE,"E23.top")])]}),makeQuery(id+"F23.opExtrude","CAP_FACE",FACE,{"disambiguationData":[OSD([sQuery(id+"F22.wireOp",EDGE,"E30.bottom"),sQuery(id+"F22.wireOp",EDGE,"E30.top"),sQuery(id+"F22.wireOp",EDGE,"E30.left"),sQuery(id+"F22.wireOp",EDGE,"E30.right")])],"isStart":false}),makeQuery(id+"F23.opExtrude","CAP_FACE",FACE,{"disambiguationData":[OSD([sQuery(id+"F22.wireOp",EDGE,"E31.bottom"),sQuery(id+"F22.wireOp",EDGE,"E31.top"),sQuery(id+"F22.wireOp",EDGE,"E31.left"),sQuery(id+"F22.wireOp",EDGE,"E31.right"),sQuery(id+"F22.wireOp",EDGE,"E32.bottom"),sQuery(id+"F22.wireOp",EDGE,"E32.top"),sQuery(id+"F22.wireOp",EDGE,"E32.right")])],"isStart":false}),makeQuery(id+"F23.opExtrude","CAP_FACE",FACE,{"disambiguationData":[OSD([sQuery(id+"F22.wireOp",EDGE,"E33.bottom"),sQuery(id+"F22.wireOp",EDGE,"E33.top"),sQuery(id+"F22.wireOp",EDGE,"E33.left"),sQuery(id+"F22.wireOp",EDGE,"E33.right")])],"isStart":false}),makeQuery(id+"F23.opExtrude","CAP_FACE",FACE,{"disambiguationData":[OSD([sQuery(id+"F22.wireOp",EDGE,"E34.bottom"),sQuery(id+"F22.wireOp",EDGE,"E34.top"),sQuery(id+"F22.wireOp",EDGE,"E34.left"),sQuery(id+"F22.wireOp",EDGE,"E34.right"),sQuery(id+"F22.wireOp",EDGE,"E35.top"),sQuery(id+"F22.wireOp",EDGE,"E35.left"),sQuery(id+"F22.wireOp",EDGE,"E35.right")])],"isStart":false}),makeQuery(id+"F23.opExtrude","CAP_FACE",FACE,{"disambiguationData":[OSD([sQuery(id+"F22.wireOp",EDGE,"E36.bottom"),sQuery(id+"F22.wireOp",EDGE,"E36.top"),sQuery(id+"F22.wireOp",EDGE,"E36.left"),sQuery(id+"F22.wireOp",EDGE,"E36.right")])],"isStart":false})]}),makeQuery(id+"F25.opExtrude","SWEPT_FACE",FACE,{"disambiguationData":[OSD([sQuery(id+"F24.wireOp",EDGE,"E37.bottom")])]})]}),makeQuery(id+"F51.opExtrude","SWEPT_FACE",FACE,{"disambiguationData":[OSD([sQuery(id+"F50.wireOp",EDGE,"E70.bottom")])]})]});
            extrude(context, id + "F53", {"entities" : qUnion([Q0]), "operationType" : NewBodyOperationType.ADD, "endBound" : BoundingType.UP_TO_SURFACE, "endBoundEntityFace" : qUnion([Q1]), "depth" : 25.4 * mm});
        }
        {
            var Q0;
            {var subQ1=sQuery(id+"F38.wireOp",EDGE,"E52.right");var subQ5=sQuery(id+"F42.wireOp",EDGE,"E57.bottom");Q0=makeQuery(id+"F43.boolean.opBoolean","SPLIT",FACE,{"disambiguationData":[TD([makeQuery(id+"F39.opExtrude","SWEPT_FACE",FACE,{"disambiguationData":[OSD([subQ1])]})])],"derivedFrom":makeQuery(id+"F43.opExtrude","SWEPT_FACE",FACE,{"disambiguationData":[OSD([subQ5])]})});}
            var sketch = newSketch(context, id + "F54", { "sketchPlane" : qUnion([Q0])});
            skLineSegment(sketch, "E75.bottom", {"start": v(228.6, 1771.65) * mm, "end": v(1143, 1771.65) * mm});
            skLineSegment(sketch, "E75.top", {"start": v(228.6, 1708.15) * mm, "end": v(1143, 1708.15) * mm});
            skLineSegment(sketch, "E75.left", {"start": v(228.6, 1771.65) * mm, "end": v(228.6, 1708.15) * mm});
            skLineSegment(sketch, "E75.right", {"start": v(1143, 1771.65) * mm, "end": v(1143, 1708.15) * mm});
            skSolve(sketch);
        }
        {
            var Q0;
            {var subQ0=sQuery(id+"F54.wireOp",EDGE,"E75.top");Q0=makeQuery(id+"F54.imprint","IMPRINT",FACE,{"disambiguationData":[TD([[makeQuery(id+"F54.imprint","IMPRINT",EDGE,{"derivedFrom":subQ0}),1.0]])]});}
            var Q1;
            {var subQ0=sQuery(id+"F54.wireOp",EDGE,"E75.bottom");Q1=makeQuery(id+"F54.imprint","IMPRINT",FACE,{"disambiguationData":[TD([[makeQuery(id+"F54.imprint","IMPRINT",EDGE,{"derivedFrom":subQ0}),1.0]])]});}
            extrude(context, id + "F55", {"entities" : qUnion([Q0, Q1]), "operationType" : NewBodyOperationType.ADD, "depth" : 19.05 * mm});
        }
    });
